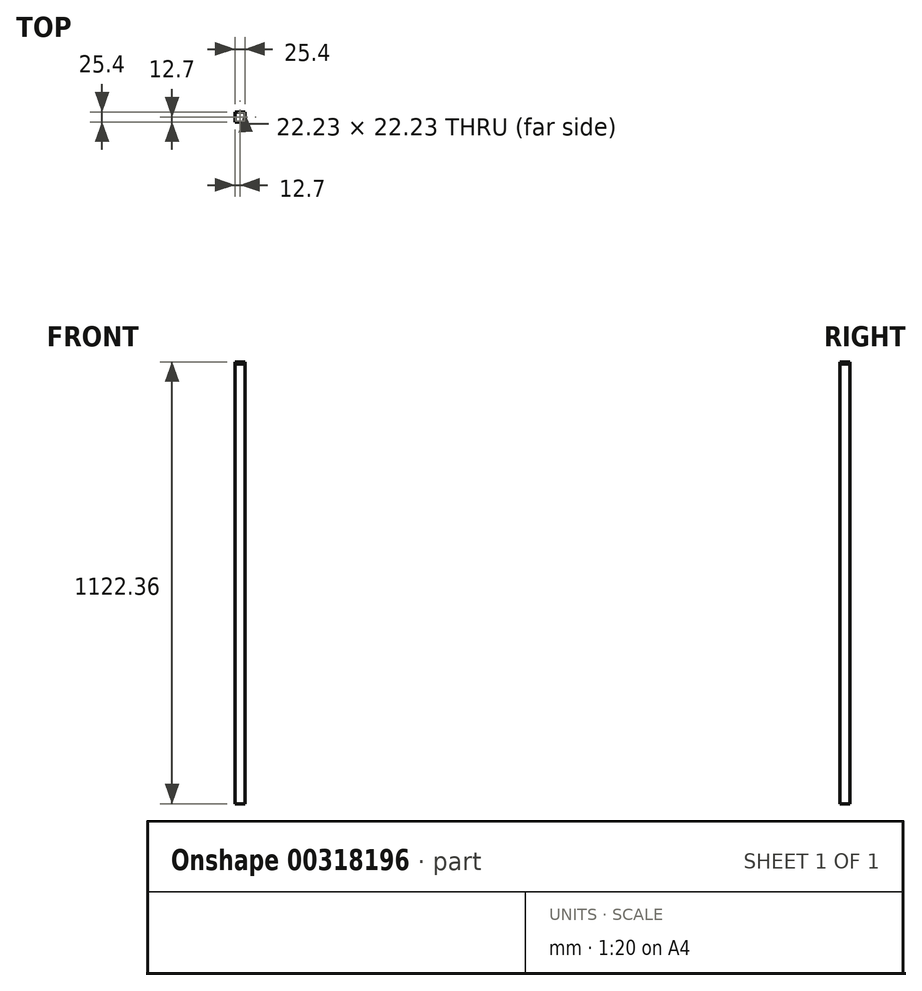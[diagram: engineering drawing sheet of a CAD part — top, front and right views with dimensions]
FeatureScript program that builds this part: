
annotation { "Feature Type Name" : "Feature", "Feature Type Description" : "" }
export const myFeature = defineFeature(function(context is Context, id is Id, definition is map)
    precondition{}
    {
        {
            var Q0;
            Q0=qCreatedBy(makeId("Top.planeOp"),FACE);
            var sketch = newSketch(context, id + "F0", { "sketchPlane" : qUnion([Q0])});
            skLineSegment(sketch, "E0.bottom", {"start": v(-12.7, 12.7) * mm, "end": v(12.7, 12.7) * mm});
            skLineSegment(sketch, "E0.top", {"start": v(-12.7, -12.7) * mm, "end": v(12.7, -12.7) * mm});
            skLineSegment(sketch, "E0.left", {"start": v(-12.7, 12.7) * mm, "end": v(-12.7, -12.7) * mm});
            skLineSegment(sketch, "E0.right", {"start": v(12.7, 12.7) * mm, "end": v(12.7, -12.7) * mm});
            skPoint(sketch, "E0.middle", {"position": v(0, 0) * mm});
            skLineSegment(sketch, "E1.0", {"start": v(-11.11, 11.11) * mm, "end": v(-11.11, -11.11) * mm});
            skLineSegment(sketch, "E1.1", {"start": v(-11.11, 11.11) * mm, "end": v(11.11, 11.11) * mm});
            skLineSegment(sketch, "E1.2", {"start": v(11.11, 11.11) * mm, "end": v(11.11, -11.11) * mm});
            skLineSegment(sketch, "E1.3", {"start": v(-11.11, -11.11) * mm, "end": v(11.11, -11.11) * mm});
            skSolve(sketch);
        }
        {
            var Q0;
            Q0 = qSketchRegion(id + "F0", true);
            extrude(context, id + "F1", {"entities" : qUnion([Q0]), "endBound" : BoundingType.SYMMETRIC, "depth" : 1117.6 * mm});
        }
        {
            var Q0;
            Q0=makeQuery(id+"F1.opExtrude","CAP_FACE",FACE,{"disambiguationData":[OSD([sQuery(id+"F0.wireOp",EDGE,"E0.bottom"),sQuery(id+"F0.wireOp",EDGE,"E0.top"),sQuery(id+"F0.wireOp",EDGE,"E0.left"),sQuery(id+"F0.wireOp",EDGE,"E0.right"),sQuery(id+"F0.wireOp",EDGE,"E1.0"),sQuery(id+"F0.wireOp",EDGE,"E1.1"),sQuery(id+"F0.wireOp",EDGE,"E1.2"),sQuery(id+"F0.wireOp",EDGE,"E1.3")])],"isStart":false});
            var sketch = newSketch(context, id + "F2", { "sketchPlane" : qUnion([Q0])});
            skLineSegment(sketch, "E2.bottom", {"start": v(-12.7, -12.7) * mm, "end": v(12.7, -12.7) * mm});
            skLineSegment(sketch, "E2.top", {"start": v(-12.7, 12.7) * mm, "end": v(12.7, 12.7) * mm});
            skLineSegment(sketch, "E2.left", {"start": v(-12.7, -12.7) * mm, "end": v(-12.7, 12.7) * mm});
            skLineSegment(sketch, "E2.right", {"start": v(12.7, -12.7) * mm, "end": v(12.7, 12.7) * mm});
            skSolve(sketch);
        }
        {
            var Q0;
            Q0 = qSketchRegion(id + "F2", true);
            extrude(context, id + "F3", {"entities" : qUnion([Q0]), "depth" : 4.76 * mm});
        }
    });
